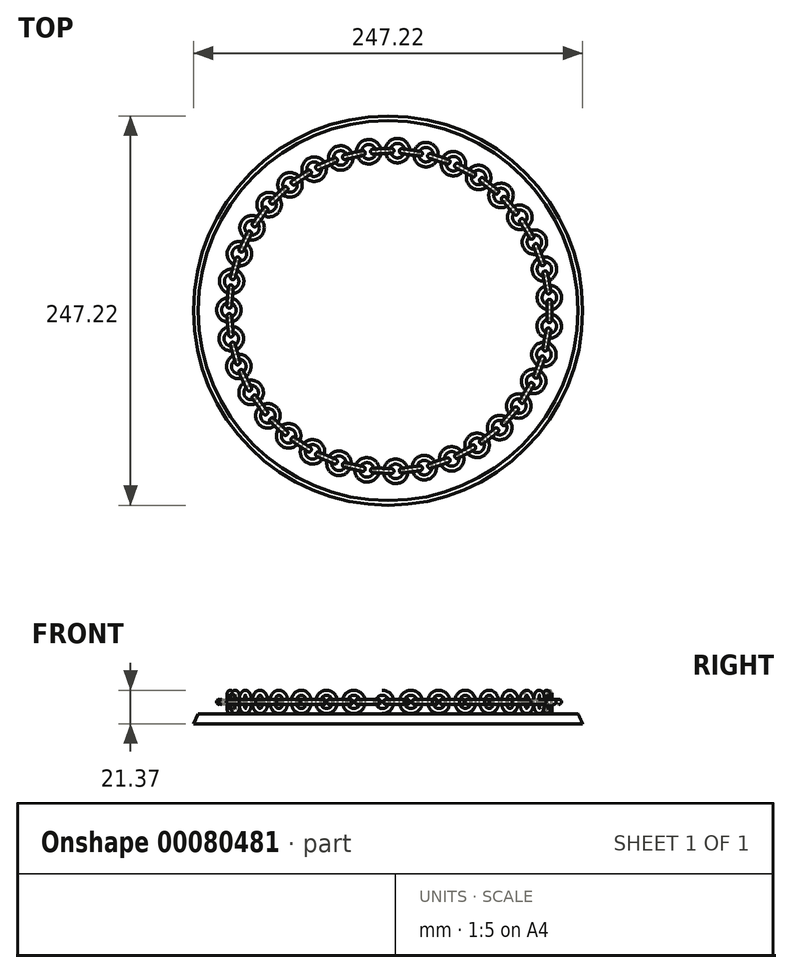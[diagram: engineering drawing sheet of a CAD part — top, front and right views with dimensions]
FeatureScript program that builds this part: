
annotation { "Feature Type Name" : "Feature", "Feature Type Description" : "" }
export const myFeature = defineFeature(function(context is Context, id is Id, definition is map)
    precondition{}
    {
        {
            var Q0;
            Q0=qCreatedBy(makeId("Top.planeOp"),FACE);
            var sketch = newSketch(context, id + "F0", { "sketchPlane" : qUnion([Q0])});
            skCircle(sketch, "E0", {"center": v(0, 0) * mm, "radius": 101.6 * mm, "construction": true});
            skSolve(sketch);
        }
        {
            var Q0;
            Q0=qCreatedBy(makeId("Front.planeOp"),FACE);
            var sketch = newSketch(context, id + "F1", { "sketchPlane" : qUnion([Q0])});
            skCircle(sketch, "E1", {"center": v(101.6, 5.81) * mm, "radius": 1.59 * mm});
            skSolve(sketch);
        }
        {
            var Q0;
            Q0=qCreatedBy(makeId("Front.planeOp"),FACE);
            var sketch = newSketch(context, id + "F2", { "sketchPlane" : qUnion([Q0])});
            skLineSegment(sketch, "E2", {"start": v(92.2, 0) * mm, "end": v(111.93, 0) * mm, "construction": true});
            skSolve(sketch);
        }
        {
            var Q0;
            Q0 = qSketchRegion(id + "F1", true);
            var Q1;
            Q1=sQuery(id+"F2.wireOp",EDGE,"E2");
            revolve(context, id + "F3", {"entities" : qUnion([Q0]), "axis" : qUnion([Q1]), "revolveType" : RevolveType.FULL});
        }
        {
            var Q0;
            Q0=qCreatedBy(makeId("Right.planeOp"),FACE);
            cPlane(context, id + "F4", {"entities" : qUnion([Q0]), "cplaneType" : CPlaneType.OFFSET, "offset" : 101.6 * mm, "width" : 152.4 * mm, "height" : 152.4 * mm});
        }
        {
            var Q0;
            Q0=qCreatedBy(id+"F4.planeOp",FACE);
            var sketch = newSketch(context, id + "F5", { "sketchPlane" : qUnion([Q0])});
            skCircle(sketch, "E3", {"center": v(14.77, 0) * mm, "radius": 1.59 * mm});
            skLineSegment(sketch, "E4", {"start": v(8.56, 6.71) * mm, "end": v(8.56, -7.9) * mm, "construction": true});
            skSolve(sketch);
        }
        {
            var Q0;
            Q0 = qSketchRegion(id + "F5", true);
            var Q1;
            Q1=sQuery(id+"F5.wireOp",EDGE,"E4");
            revolve(context, id + "F6", {"operationType" : NewBodyOperationType.ADD, "entities" : qUnion([Q0]), "axis" : qUnion([Q1]), "revolveType" : RevolveType.FULL});
        }
        {
            var Q0;
            Q0=makeQuery(id+"F3.opRevolve","SWEPT_BODY",BODY,{"disambiguationData":[OSD([sQuery(id+"F1.wireOp",EDGE,"E1")])]});
            var Q1;
            Q1=makeQuery(id+"F6.opRevolve","SWEPT_BODY",BODY,{"disambiguationData":[OSD([sQuery(id+"F5.wireOp",EDGE,"E3")])]});
            var Q2;
            Q2=sQuery(id+"F0.wireOp",EDGE,"E0");
            circularPattern(context, id + "F7", {"entities" : qUnion([Q0, Q1]), "axis" : qUnion([Q2]), "angle" : 360 * degree, "instanceCount" : 35, "equalSpace" : true});
        }
        {
            var Q0;
            Q0=qCreatedBy(makeId("Top.planeOp"),FACE);
            cPlane(context, id + "F8", {"entities" : qUnion([Q0]), "cplaneType" : CPlaneType.OFFSET, "offset" : 7.62 * mm, "oppositeDirection" : true, "width" : 152.4 * mm, "height" : 152.4 * mm});
        }
        {
            var Q0;
            Q0=qCreatedBy(id+"F8.planeOp",FACE);
            var sketch = newSketch(context, id + "F9", { "sketchPlane" : qUnion([Q0])});
            skCircle(sketch, "E5", {"center": v(-0.82, 0.19) * mm, "radius": 120.65 * mm});
            skSolve(sketch);
        }
        {
            var Q0;
            Q0 = qSketchRegion(id + "F9", true);
            extrude(context, id + "F10", {"entities" : qUnion([Q0]), "oppositeDirection" : true, "depth" : 6.35 * mm, "hasDraft" : true, "draftAngle" : 25 * degree});
        }
    });
